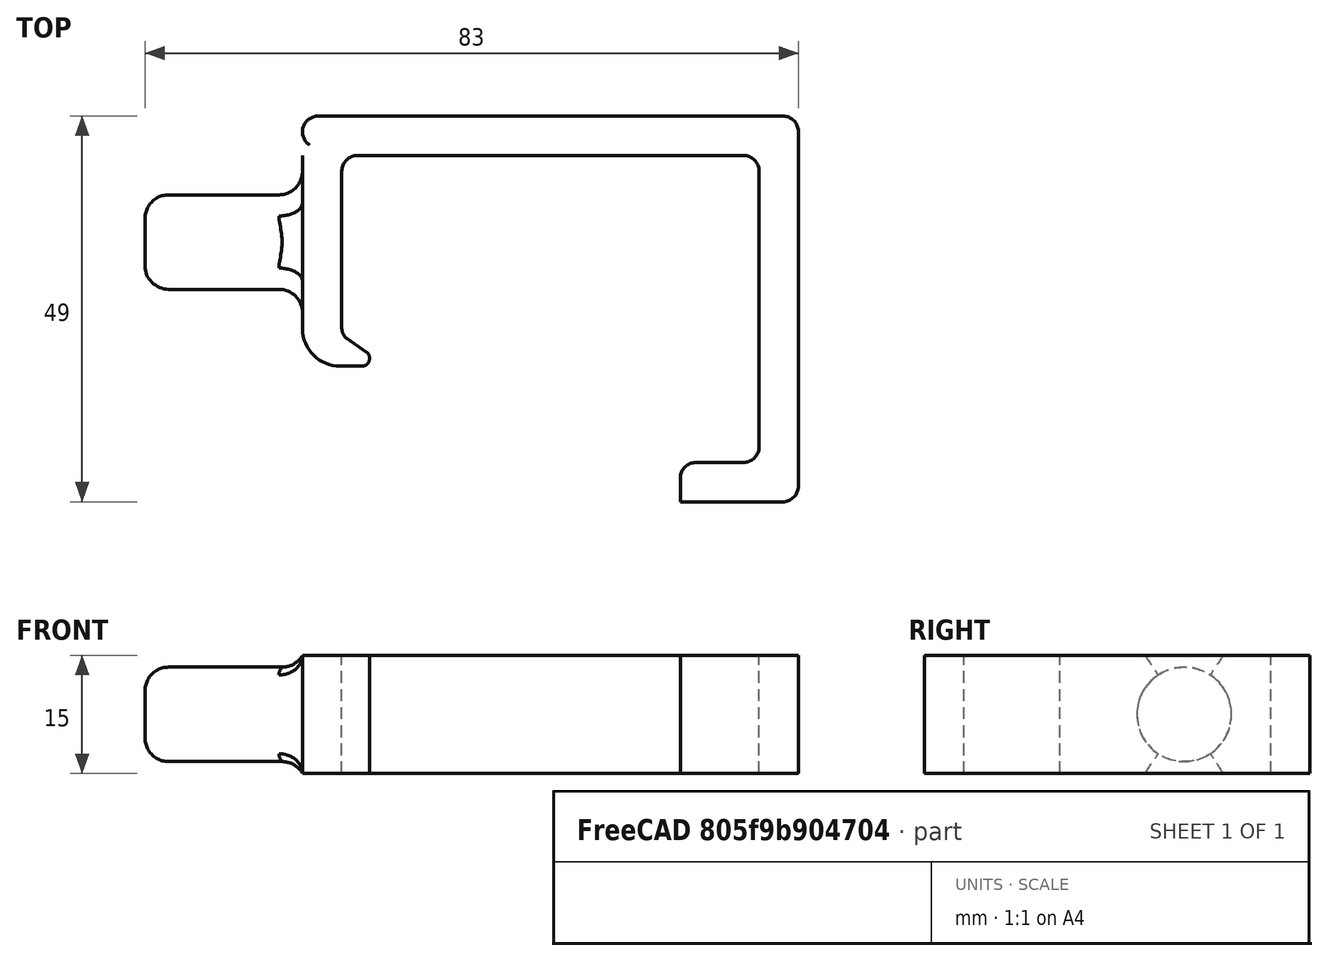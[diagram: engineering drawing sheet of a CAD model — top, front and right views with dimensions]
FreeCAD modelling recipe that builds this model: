
FCSTD DOCUMENT  (FreeCAD 0.19R24291 (Git))
Label: bed headboard hook round
License: All rights reserved
LicenseURL: http://en.wikipedia.org/wiki/All_rights_reserved
objects: Sketcher::SketchObject×2, PartDesign::Pad×2, PartDesign::Fillet×1, PartDesign::Body×1
note: 9 computed .brp shape members not serialized (recipe doc carries the construction recipe); baked Part::Feature solids carry a one-line shape summary decoded from their .brp

FEATURE [Sketcher::SketchObject] Sketch
  FullyConstrained = true
  MapMode = 5
  Support = -> [XY_Plane]
  sketch-geometry (23):
    g0: LineSegment StartX=-6 StartY=-39 StartZ=0 EndX=-9e-16 EndY=-39 EndZ=0
    g1: LineSegment StartX=2 StartY=-37 StartZ=0 EndX=2 EndY=-2 EndZ=0
    g2: LineSegment StartX=-51 StartY=-2 StartZ=0 EndX=-51 EndY=-22 EndZ=0
    g3: LineSegment StartX=-56 StartY=-22 StartZ=0 EndX=-56 EndY=0 EndZ=0
    g4: LineSegment StartX=7 StartY=3 StartZ=0 EndX=7 EndY=-42 EndZ=0
    g5: LineSegment StartX=5 StartY=-44 StartZ=0 EndX=-8 EndY=-44 EndZ=0
    g6: LineSegment StartX=-8 StartY=-44 StartZ=0 EndX=-8 EndY=-41 EndZ=0
    g7: LineSegment StartX=-49 StartY=0 StartZ=0 EndX=0 EndY=0 EndZ=0
    g8: LineSegment StartX=5 StartY=5 StartZ=0 EndX=-54 EndY=5 EndZ=0
    g9: ArcOfCircle CenterX=-2e-16 CenterY=-2 CenterZ=0 NormalX=0 NormalY=0 NormalZ=1 AngleXU=0 Radius=2 StartAngle=0 EndAngle=1.5708
    g10: ArcOfCircle CenterX=5 CenterY=3 CenterZ=0 NormalX=0 NormalY=0 NormalZ=1 AngleXU=0 Radius=2 StartAngle=0 EndAngle=1.5708
    g11: ArcOfCircle CenterX=5 CenterY=-42 CenterZ=0 NormalX=0 NormalY=0 NormalZ=1 AngleXU=0 Radius=2 StartAngle=4.71239 EndAngle=6.28319
    g12: ArcOfCircle CenterX=-6 CenterY=-41 CenterZ=0 NormalX=0 NormalY=0 NormalZ=1 AngleXU=0 Radius=2 StartAngle=1.5708 EndAngle=3.14159
    g13: ArcOfCircle CenterX=-49 CenterY=-2 CenterZ=0 NormalX=0 NormalY=0 NormalZ=1 AngleXU=0 Radius=2 StartAngle=1.5708 EndAngle=3.14159
    g14: ArcOfCircle CenterX=-2e-16 CenterY=-37 CenterZ=0 NormalX=0 NormalY=0 NormalZ=1 AngleXU=0 Radius=2 StartAngle=4.71239 EndAngle=6.28319
    g15: LineSegment StartX=-50.3604 StartY=-23.2287 StartZ=0 EndX=-47.9029 EndY=-24.9495 EndZ=0
    g16: LineSegment StartX=-48.4765 StartY=-26.7686 StartZ=0 EndX=-51.2314 EndY=-26.7686 EndZ=0
    g17: ArcOfCircle CenterX=-48.4765 CenterY=-25.7686 CenterZ=0 NormalX=0 NormalY=0 NormalZ=1 AngleXU=0 Radius=1 StartAngle=4.71239 EndAngle=7.24312
    g18: ArcOfCircle CenterX=-49.5 CenterY=-22 CenterZ=0 NormalX=0 NormalY=0 NormalZ=1 AngleXU=0 Radius=1.5 StartAngle=3.14159 EndAngle=4.10152
    g19: ArcOfCircle CenterX=-51.2314 CenterY=-22 CenterZ=0 NormalX=0 NormalY=0 NormalZ=1 AngleXU=0 Radius=4.76861 StartAngle=3.14159 EndAngle=4.71239
    g20: LineSegment StartX=-56 StartY=0 StartZ=0 EndX=-56 EndY=3 EndZ=0
    g21: LineSegment StartX=-56 StartY=0 StartZ=0 EndX=-56 EndY=3 EndZ=0
    g22: ArcOfCircle CenterX=-54 CenterY=3 CenterZ=0 NormalX=0 NormalY=0 NormalZ=1 AngleXU=0 Radius=2 StartAngle=1.5708 EndAngle=3.14159
  constraints (57):
    c: Horizontal(g0)
    c: Vertical(g3)
    c: Vertical(g4)
    c: Horizontal(g5)
    c: Coincident(g5,g6)
    c: Vertical(g6)
    c: Vertical(g1)
    c: Vertical(g2)
    c: Horizontal(g7)
    c: Horizontal(g8)
    c: PointOnObject(g3,g-1)
    c: Tangent(g1,g9) = -1.5708
    c: Tangent(g7,g9) = 1.5708
    c: Tangent(g8,g10) = -1.5708
    c: Tangent(g4,g10) = 1.5708
    c: Tangent(g4,g11) = 1.5708
    c: Tangent(g5,g11) = 1.5708
    c: Tangent(g0,g12) = 1.5708
    c: Tangent(g6,g12) = 1.5708
    c: Tangent(g7,g13) = 1.5708
    c: Tangent(g2,g13) = -1.5708
    c: Tangent(g0,g14) = -1.5708
    c: Tangent(g1,g14) = -1.5708
    c: DistanceY(g0,g7) = 39
    c: DistanceX(g6,g1) = 10
    c: DistanceX(g3,g2) = 5
    c: DistanceY(g5,g0) = 5
    c: DistanceX(g1,g4) = 5
    c: Coincident(g-1,g7)
    c: DistanceX(g2,g1) = 53
    c: Horizontal(g16)
    c: Tangent(g15,g17) = 1.5708
    c: Tangent(g16,g17) = 1.5708
    c: Angle(g15,g2) = 2.18166
    c: Diameter(g17) = 2
    c: Tangent(g2,g18) = -1.5708
    c: Tangent(g15,g18) = -1.5708
    c: DistanceY(g18,g7) = 22
    c: Tangent(g19,g3) = 1.5708
    c: Distance(g15) = 3
    c: Diameter(g18) = 3
    c: Horizontal(g3,g2)
    c: Tangent(g19,g16) = 1.5708
    c: Equal(g13,g10)
    c: Equal(g10,g9)
    c: Equal(g9,g14)
    c: Equal(g14,g11)
    c: Equal(g11,g12)
    c: Radius(g13) = 2
    c: Coincident(g3,g20)
    c: Vertical(g20)
    c: Coincident(g3,g21)
    c: Tangent(g8,g22) = -1.5708
    c: Tangent(g20,g22) = 1.5708
    c: Equal(g10,g22)
    c: Coincident(g20,g21)
    c: DistanceY(g3,g8) = 5
FEATURE [PartDesign::Pad] Pad
  Direction = (0,0,1)
  Length = 15
  Length2 = 100
  Profile = -> Sketch
  Type = 0
FEATURE [Sketcher::SketchObject] Sketch002
  ExternalGeometry = -> [Pad,Sketch]
  FullyConstrained = true
  MapMode = 5
  Placement = pos=(-56,0,0) rot=(0.57735,-0.57735,-0.57735;2.0944rad)
  Support = -> [Pad]
  sketch-geometry (1):
    g0: Circle CenterX=11 CenterY=7.5 CenterZ=0 NormalX=0 NormalY=0 NormalZ=1 AngleXU=0 Radius=6
  constraints (2):
    c: Radius(g0) = 6
    c: Symmetric(g-5,g-6,g0)
FEATURE [PartDesign::Pad] Pad001
  BaseFeature = -> Pad
  Direction = (1,1,1)
  Length = 20
  Length2 = 100
  Profile = -> Sketch002
  Type = 0
FEATURE [PartDesign::Fillet] Fillet
  Base = -> Pad001 [Face7]
  BaseFeature = -> Pad001
  Radius = 3
  SupportTransform = false
FEATURE [PartDesign::Body] Body
  Group = -> [Sketch,Pad,Sketch002,Pad001,Fillet]
  Origin = -> Origin
  Tip = -> Fillet
